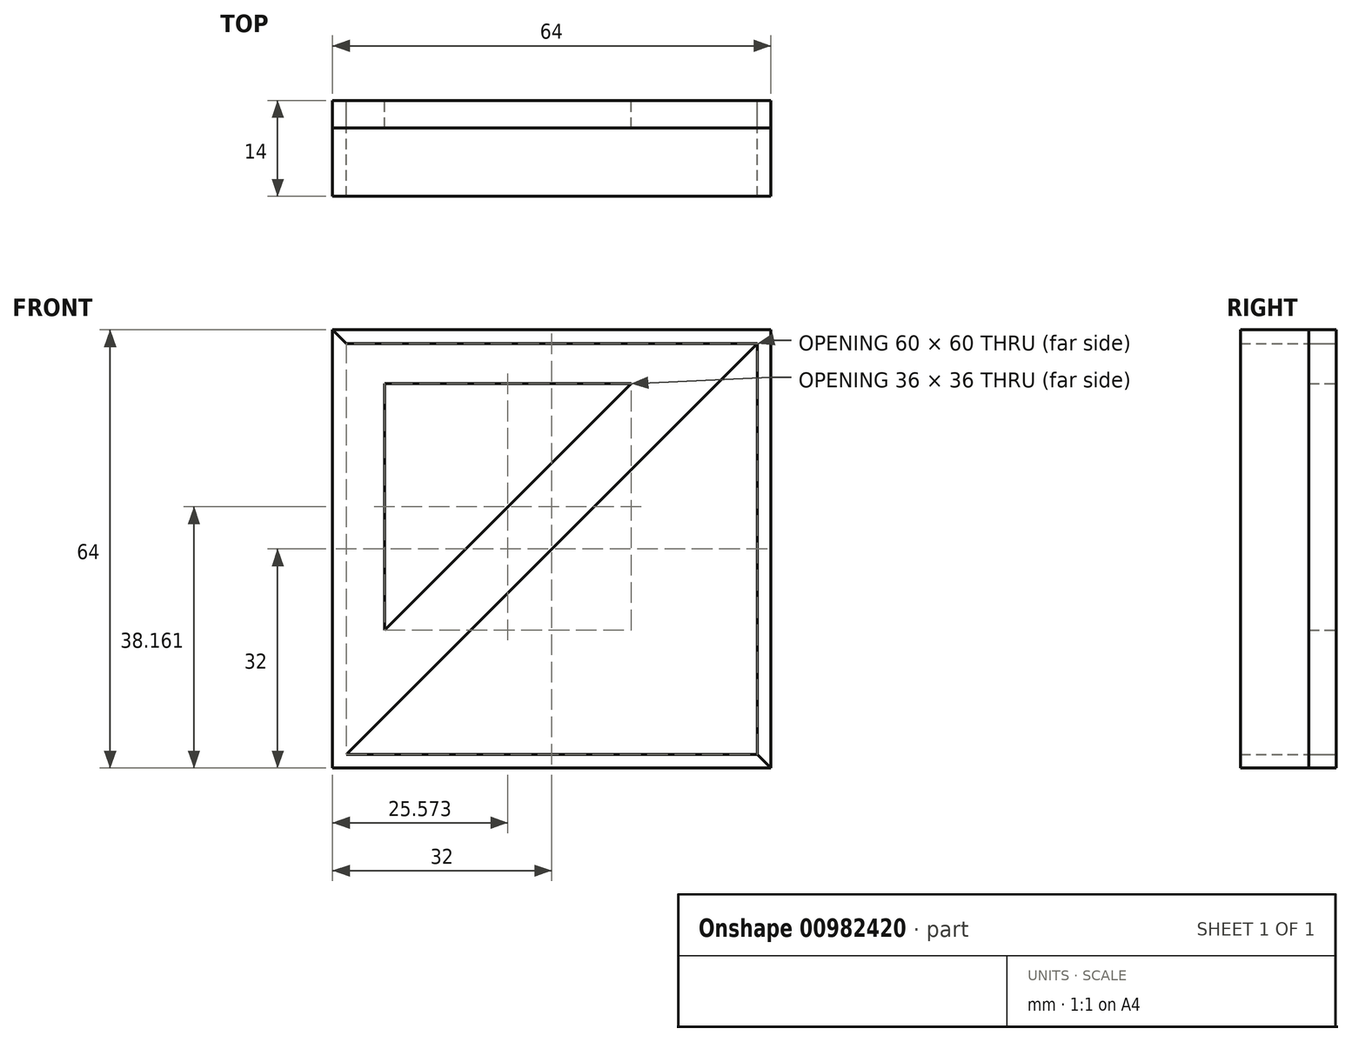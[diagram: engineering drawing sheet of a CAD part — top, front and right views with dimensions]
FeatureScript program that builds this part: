
annotation { "Feature Type Name" : "Feature", "Feature Type Description" : "" }
export const myFeature = defineFeature(function(context is Context, id is Id, definition is map)
    precondition{}
    {
        {
            var Q0;
            Q0=qCreatedBy(makeId("Front.planeOp"),FACE);
            var sketch = newSketch(context, id + "F0", { "sketchPlane" : qUnion([Q0])});
            skLineSegment(sketch, "E0.bottom", {"start": v(-30, 30) * mm, "end": v(30, 30) * mm});
            skLineSegment(sketch, "E0.top", {"start": v(-30, -30) * mm, "end": v(30, -30) * mm});
            skLineSegment(sketch, "E0.left", {"start": v(-30, 30) * mm, "end": v(-30, -30) * mm});
            skLineSegment(sketch, "E0.right", {"start": v(30, 30) * mm, "end": v(30, -30) * mm});
            skPoint(sketch, "E0.middle", {"position": v(0, 0) * mm});
            skLineSegment(sketch, "E1.bottom", {"start": v(-32, 32) * mm, "end": v(32, 32) * mm});
            skLineSegment(sketch, "E1.top", {"start": v(-32, -32) * mm, "end": v(32, -32) * mm});
            skLineSegment(sketch, "E1.left", {"start": v(-32, 32) * mm, "end": v(-32, -32) * mm});
            skLineSegment(sketch, "E1.right", {"start": v(32, 32) * mm, "end": v(32, -32) * mm});
            skLineSegment(sketch, "E2", {"start": v(-24.43, 24.16) * mm, "end": v(-24.43, -11.84) * mm});
            skLineSegment(sketch, "E3", {"start": v(-24.43, 24.16) * mm, "end": v(11.57, 24.16) * mm});
            skLineSegment(sketch, "E4", {"start": v(11.57, 24.16) * mm, "end": v(-24.43, -11.84) * mm});
            skLineSegment(sketch, "E5", {"start": v(-32, -32) * mm, "end": v(32, 32) * mm});
            skLineSegment(sketch, "E6", {"start": v(-30, 30) * mm, "end": v(-32, 32) * mm});
            skLineSegment(sketch, "E7", {"start": v(30, -30) * mm, "end": v(32, -32) * mm});
            skSolve(sketch);
        }
        {
            var Q0;
            {var subQ0=sQuery(id+"F0.wireOp",EDGE,"E0.bottom");Q0=makeQuery(id+"F0.imprint","IMPRINT",FACE,{"disambiguationData":[TD([[makeQuery(id+"F0.imprint","IMPRINT",EDGE,{"derivedFrom":subQ0}),1.0]])]});}
            var Q1;
            {var subQ0=sQuery(id+"F0.wireOp",EDGE,"E0.left");Q1=makeQuery(id+"F0.imprint","IMPRINT",FACE,{"disambiguationData":[TD([[makeQuery(id+"F0.imprint","IMPRINT",EDGE,{"derivedFrom":subQ0}),-1.0]])]});}
            var Q2;
            {var subQ1=sQuery(id+"F0.wireOp",EDGE,"E0.bottom");Q2=makeQuery(id+"F0.imprint","IMPRINT",FACE,{"disambiguationData":[TD([[makeQuery(id+"F0.imprint","IMPRINT",EDGE,{"derivedFrom":subQ1}),-1.0]])]});}
            var Q3;
            {var subQ0=sQuery(id+"F0.wireOp",EDGE,"E0.right");Q3=makeQuery(id+"F0.imprint","IMPRINT",FACE,{"disambiguationData":[TD([[makeQuery(id+"F0.imprint","IMPRINT",EDGE,{"derivedFrom":subQ0}),1.0]])]});}
            var Q4;
            {var subQ0=sQuery(id+"F0.wireOp",EDGE,"E0.top");Q4=makeQuery(id+"F0.imprint","IMPRINT",FACE,{"disambiguationData":[TD([[makeQuery(id+"F0.imprint","IMPRINT",EDGE,{"derivedFrom":subQ0}),-1.0]])]});}
            extrude(context, id + "F1", {"entities" : qUnion([Q0, Q1, Q2, Q3, Q4]), "depth" : 4 * mm, "offsetDistance" : 25 * mm});
        }
        {
            var Q0;
            {var subQ0=sQuery(id+"F0.wireOp",EDGE,"E0.right");Q0=makeQuery(id+"F0.imprint","IMPRINT",FACE,{"disambiguationData":[TD([[makeQuery(id+"F0.imprint","IMPRINT",EDGE,{"derivedFrom":subQ0}),1.0]])]});}
            var Q1;
            {var subQ0=sQuery(id+"F0.wireOp",EDGE,"E0.bottom");Q1=makeQuery(id+"F0.imprint","IMPRINT",FACE,{"disambiguationData":[TD([[makeQuery(id+"F0.imprint","IMPRINT",EDGE,{"derivedFrom":subQ0}),1.0]])]});}
            extrude(context, id + "F2", {"entities" : qUnion([Q0, Q1]), "depth" : 14 * mm, "offsetDistance" : 25 * mm});
        }
    });
